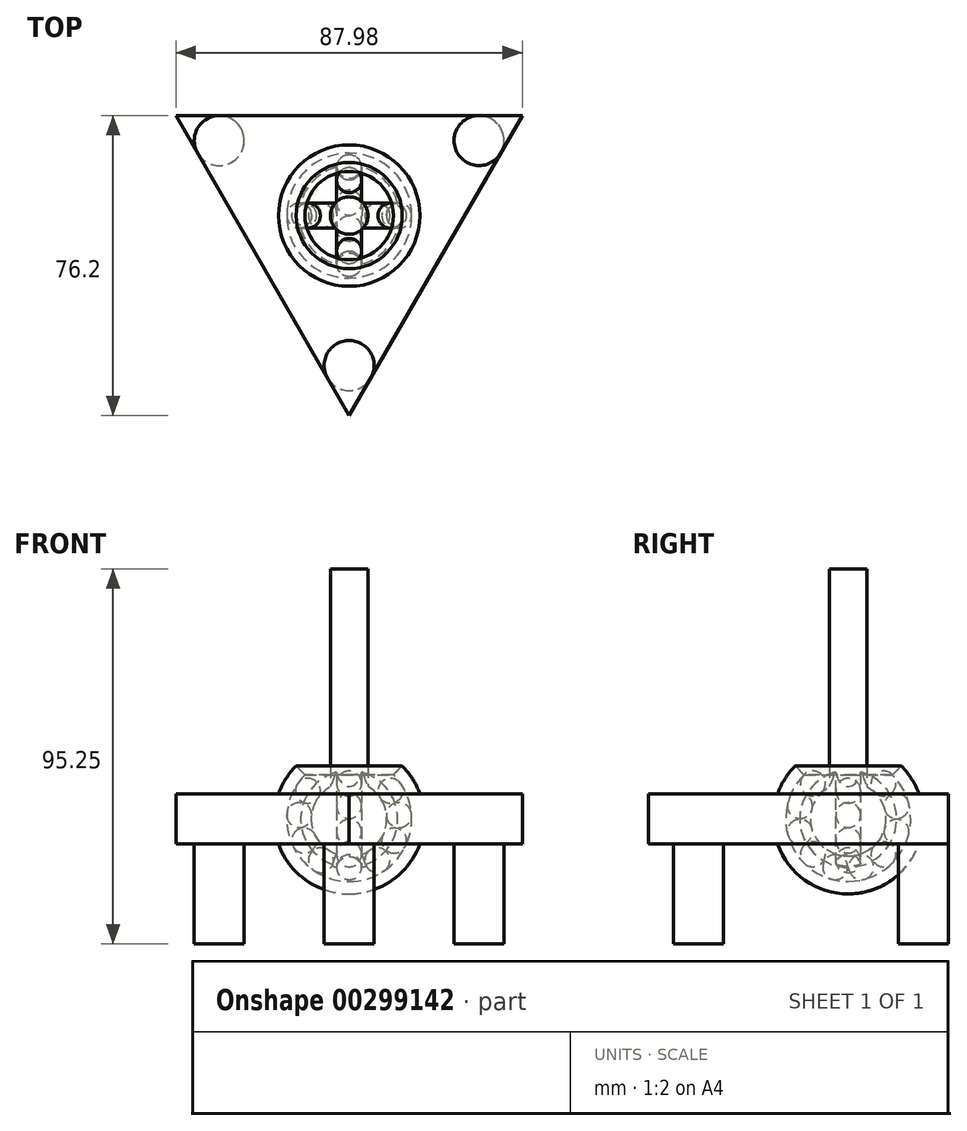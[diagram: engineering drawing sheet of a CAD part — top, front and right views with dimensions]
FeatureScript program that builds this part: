
annotation { "Feature Type Name" : "Feature", "Feature Type Description" : "" }
export const myFeature = defineFeature(function(context is Context, id is Id, definition is map)
    precondition{}
    {
        {
            var Q0;
            Q0=qCreatedBy(makeId("Front.planeOp"),FACE);
            var sketch = newSketch(context, id + "F0", { "sketchPlane" : qUnion([Q0])});
            skArc(sketch, "E0", {"start": v(0, -12.7) * mm, "mid": v(12.7, 0) * mm, "end": v(0, 12.7) * mm});
            skLineSegment(sketch, "E1", {"start": v(0, 12.7) * mm, "end": v(0, -12.7) * mm});
            skSolve(sketch);
        }
        {
            var Q0;
            Q0=makeQuery(id+"F0.imprint","IMPRINT",FACE,{"disambiguationData":[TD([[makeQuery(id+"F0.imprint","IMPRINT",EDGE,{"derivedFrom":sQuery(id+"F0.wireOp",EDGE,"E0")}),1.0]])]});
            var Q1;
            Q1=sQuery(id+"F0.wireOp",EDGE,"E1");
            revolve(context, id + "F1", {"entities" : qUnion([Q0]), "axis" : qUnion([Q1]), "revolveType" : RevolveType.FULL});
        }
        {
            var Q0;
            Q0=qCreatedBy(makeId("Right.planeOp"),FACE);
            var sketch = newSketch(context, id + "F2", { "sketchPlane" : qUnion([Q0])});
            skCircle(sketch, "E2", {"center": v(0, 0) * mm, "radius": 12.7 * mm});
            skSolve(sketch);
        }
        {
            var Q0;
            Q0=qCreatedBy(makeId("Top.planeOp"),FACE);
            var sketch = newSketch(context, id + "F3", { "sketchPlane" : qUnion([Q0])});
            skCircle(sketch, "E3", {"center": v(0, -12.7) * mm, "radius": 3.18 * mm});
            skPoint(sketch, "E4.center", {"position": v(0, 0) * mm});
            skSolve(sketch);
        }
        {
            var Q0;
            Q0=makeQuery(id+"F3.imprint","IMPRINT",FACE,{"disambiguationData":[TD([[makeQuery(id+"F3.imprint","IMPRINT",EDGE,{"derivedFrom":sQuery(id+"F3.wireOp",EDGE,"E3")}),1.0]])]});
            var Q1;
            Q1=sQuery(id+"F2.wireOp",EDGE,"E2");
            revolve(context, id + "F4", {"operationType" : NewBodyOperationType.REMOVE, "entities" : qUnion([Q0]), "axis" : qUnion([Q1]), "revolveType" : RevolveType.FULL, "oppositeDirection" : true});
        }
        {
            var Q0;
            Q0=qCreatedBy(makeId("Right.planeOp"),FACE);
            var sketch = newSketch(context, id + "F5", { "sketchPlane" : qUnion([Q0])});
            skLineSegment(sketch, "E5", {"start": v(0, 0) * mm, "end": v(0, 67.3) * mm, "construction": true});
            skSolve(sketch);
        }
        {
            var Q0;
            Q0=qCreatedBy(makeId("Right.planeOp"),FACE);
            var sketch = newSketch(context, id + "F6", { "sketchPlane" : qUnion([Q0])});
            skArc(sketch, "E6", {"start": v(11.23, 11.23) * mm, "mid": v(6.74, 11.23) * mm, "end": v(6.74, 6.74) * mm});
            skLineSegment(sketch, "E7", {"start": v(8.98, 8.98) * mm, "end": v(0, 0) * mm, "construction": true});
            skLineSegment(sketch, "E8", {"start": v(0, 0) * mm, "end": v(0, 12.71) * mm, "construction": true});
            skLineSegment(sketch, "E9", {"start": v(6.74, 6.74) * mm, "end": v(11.23, 11.23) * mm});
            skSolve(sketch);
        }
        {
            var Q0;
            Q0=makeQuery(id+"F6.imprint","IMPRINT",FACE,{"disambiguationData":[TD([[makeQuery(id+"F6.imprint","IMPRINT",EDGE,{"derivedFrom":sQuery(id+"F6.wireOp",EDGE,"E6")}),1.0]])]});
            var Q1;
            Q1=sQuery(id+"F6.wireOp",EDGE,"E7");
            revolve(context, id + "F7", {"entities" : qUnion([Q0]), "axis" : qUnion([Q1]), "revolveType" : RevolveType.FULL});
        }
        {
            var Q0;
            Q0=makeQuery(id+"F7.opRevolve","SWEPT_BODY",BODY,{"disambiguationData":[OSD([sQuery(id+"F6.wireOp",EDGE,"E6"),sQuery(id+"F6.wireOp",EDGE,"E9")])]});
            var Q1;
            Q1=makeQuery(id+"F4.boolean.opBoolean","COPY",FACE,{"derivedFrom":makeQuery(id+"F4.opRevolve","SWEPT_FACE",FACE,{"disambiguationData":[OSD([sQuery(id+"F3.wireOp",EDGE,"E3")])]})});
            circularPattern(context, id + "F8", {"entities" : qUnion([Q0]), "axis" : qUnion([Q1]), "angle" : 270 * degree, "instanceCount" : 10, "equalSpace" : true});
        }
        {
            var Q0;
            Q0=qCreatedBy(makeId("Top.planeOp"),FACE);
            var sketch = newSketch(context, id + "F9", { "sketchPlane" : qUnion([Q0])});
            skCircle(sketch, "E10", {"center": v(12.7, 0) * mm, "radius": 3.18 * mm});
            skSolve(sketch);
        }
        {
            var Q0;
            Q0=qCreatedBy(makeId("Right.planeOp"),FACE);
            var sketch = newSketch(context, id + "F10", { "sketchPlane" : qUnion([Q0])});
            skLineSegment(sketch, "E11", {"start": v(-25.97, 0) * mm, "end": v(39.67, 0) * mm, "construction": true});
            skSolve(sketch);
        }
        {
            var Q0;
            Q0=makeQuery(id+"F9.imprint","IMPRINT",FACE,{"disambiguationData":[TD([[makeQuery(id+"F9.imprint","IMPRINT",EDGE,{"derivedFrom":sQuery(id+"F9.wireOp",EDGE,"E10")}),1.0]])]});
            var Q1;
            Q1=sQuery(id+"F10.wireOp",EDGE,"E11");
            revolve(context, id + "F11", {"operationType" : NewBodyOperationType.REMOVE, "entities" : qUnion([Q0]), "axis" : qUnion([Q1]), "revolveType" : RevolveType.TWO_DIRECTIONS, "oppositeDirection" : true, "angle" : 250 * degree, "angleBack" : 290 * degree});
        }
        {
            var Q0;
            Q0=qCreatedBy(makeId("Top.planeOp"),FACE);
            var sketch = newSketch(context, id + "F12", { "sketchPlane" : qUnion([Q0])});
            skCircle(sketch, "E12", {"center": v(0, 0) * mm, "radius": 4.76 * mm});
            skSolve(sketch);
        }
        {
            var Q0;
            Q0 = qSketchRegion(id + "F12", true);
            extrude(context, id + "F13", {"entities" : qUnion([Q0]), "operationType" : NewBodyOperationType.ADD, "depth" : 63.5 * mm});
        }
        {
            var Q0;
            Q0=qCreatedBy(makeId("Front.planeOp"),FACE);
            var sketch = newSketch(context, id + "F14", { "sketchPlane" : qUnion([Q0])});
            skArc(sketch, "E13", {"start": v(5.38, -7.86) * mm, "mid": v(4.55, -12.28) * mm, "end": v(8.96, -13.1) * mm});
            skLineSegment(sketch, "E14", {"start": v(7.17, -10.48) * mm, "end": v(0, 0) * mm, "construction": true});
            skLineSegment(sketch, "E15", {"start": v(0, 0) * mm, "end": v(0, -18.63) * mm, "construction": true});
            skLineSegment(sketch, "E16", {"start": v(5.38, -7.86) * mm, "end": v(8.96, -13.1) * mm});
            skSolve(sketch);
        }
        {
            var Q0;
            Q0=qCreatedBy(makeId("Top.planeOp"),FACE);
            var sketch = newSketch(context, id + "F15", { "sketchPlane" : qUnion([Q0])});
            skLineSegment(sketch, "E17", {"start": v(0, 30.24) * mm, "end": v(0, -29.34) * mm, "construction": true});
            skSolve(sketch);
        }
        {
            var Q0;
            Q0 = qSketchRegion(id + "F14", true);
            var Q1;
            Q1=sQuery(id+"F14.wireOp",EDGE,"E14");
            revolve(context, id + "F16", {"entities" : qUnion([Q0]), "axis" : qUnion([Q1]), "revolveType" : RevolveType.FULL});
        }
        {
            var Q0;
            Q0=makeQuery(id+"F16.opRevolve","SWEPT_BODY",BODY,{"disambiguationData":[OSD([sQuery(id+"F14.wireOp",EDGE,"E13"),sQuery(id+"F14.wireOp",EDGE,"E16")])]});
            var Q1;
            Q1=sQuery(id+"F15.wireOp",EDGE,"E17");
            circularPattern(context, id + "F17", {"entities" : qUnion([Q0]), "axis" : qUnion([Q1]), "angle" : 30 * degree, "instanceCount" : 4});
        }
        {
            var Q0;
            Q0=makeQuery(id+"F17.opPattern","COPY",BODY,{"derivedFrom":makeQuery(id+"F16.opRevolve","SWEPT_BODY",BODY,{"disambiguationData":[OSD([sQuery(id+"F14.wireOp",EDGE,"E13"),sQuery(id+"F14.wireOp",EDGE,"E16")])]}),"instanceName":"3"});
            var Q1;
            Q1=makeQuery(id+"F17.opPattern","COPY",BODY,{"derivedFrom":makeQuery(id+"F16.opRevolve","SWEPT_BODY",BODY,{"disambiguationData":[OSD([sQuery(id+"F14.wireOp",EDGE,"E13"),sQuery(id+"F14.wireOp",EDGE,"E16")])]}),"instanceName":"2"});
            var Q2;
            Q2=makeQuery(id+"F16.opRevolve","SWEPT_BODY",BODY,{"disambiguationData":[OSD([sQuery(id+"F14.wireOp",EDGE,"E13"),sQuery(id+"F14.wireOp",EDGE,"E16")])]});
            var Q3;
            Q3=makeQuery(id+"F17.opPattern","COPY",BODY,{"derivedFrom":makeQuery(id+"F16.opRevolve","SWEPT_BODY",BODY,{"disambiguationData":[OSD([sQuery(id+"F14.wireOp",EDGE,"E13"),sQuery(id+"F14.wireOp",EDGE,"E16")])]}),"instanceName":"1"});
            var Q4;
            Q4=qCreatedBy(makeId("Right.planeOp"),FACE);
            mirror(context, id + "F18", {"entities" : qUnion([Q0, Q1, Q2, Q3]), "mirrorPlane" : qUnion([Q4])});
        }
        {
            var Q0;
            Q0=qCreatedBy(makeId("Right.planeOp"),FACE);
            var sketch = newSketch(context, id + "F19", { "sketchPlane" : qUnion([Q0])});
            skLineSegment(sketch, "E18", {"start": v(0, -15.87) * mm, "end": v(0, -19.05) * mm});
            skArc(sketch, "E19", {"start": v(0, -15.87) * mm, "mid": v(14.67, -6.08) * mm, "end": v(11.23, 11.23) * mm});
            skArc(sketch, "E20", {"start": v(0, -19.05) * mm, "mid": v(17.6, -7.3) * mm, "end": v(13.47, 13.47) * mm});
            skLineSegment(sketch, "E21", {"start": v(11.23, 11.23) * mm, "end": v(13.47, 13.47) * mm});
            skLineSegment(sketch, "E22", {"start": v(13.47, 13.47) * mm, "end": v(0, 0) * mm, "construction": true});
            skSolve(sketch);
        }
        {
            var Q0;
            Q0 = qSketchRegion(id + "F19", true);
            var Q1;
            Q1=sQuery(id+"F19.wireOp",EDGE,"E18");
            revolve(context, id + "F20", {"entities" : qUnion([Q0]), "axis" : qUnion([Q1]), "revolveType" : RevolveType.FULL});
        }
        {
            var Q0;
            Q0=qCreatedBy(makeId("Top.planeOp"),FACE);
            var sketch = newSketch(context, id + "F21", { "sketchPlane" : qUnion([Q0])});
            skLineSegment(sketch, "E23", {"start": v(0, -50.8) * mm, "end": v(44, 25.4) * mm});
            skLineSegment(sketch, "E24", {"start": v(44, 25.4) * mm, "end": v(-44, 25.4) * mm});
            skLineSegment(sketch, "E25", {"start": v(-44, 25.4) * mm, "end": v(0, -50.8) * mm});
            skCircle(sketch, "E26", {"center": v(0, 0) * mm, "radius": 17.46 * mm});
            skSolve(sketch);
        }
        {
            var Q0;
            Q0=makeQuery(id+"F21.imprint","IMPRINT",FACE,{"disambiguationData":[TD([[makeQuery(id+"F21.imprint","IMPRINT",EDGE,{"derivedFrom":sQuery(id+"F21.wireOp",EDGE,"E23")}),1.0]])]});
            extrude(context, id + "F22", {"entities" : qUnion([Q0]), "operationType" : NewBodyOperationType.ADD, "depth" : 12.7 * mm, "symmetric" : true});
        }
        {
            var Q0;
            Q0=makeQuery(id+"F22.opExtrude","CAP_FACE",FACE,{"disambiguationData":[OSD([sQuery(id+"F21.wireOp",EDGE,"E23"),sQuery(id+"F21.wireOp",EDGE,"E24"),sQuery(id+"F21.wireOp",EDGE,"E25"),sQuery(id+"F21.wireOp",EDGE,"E26")])],"isStart":true});
            var sketch = newSketch(context, id + "F23", { "sketchPlane" : qUnion([Q0])});
            skCircle(sketch, "E27", {"center": v(0, 38.1) * mm, "radius": 6.35 * mm});
            skCircle(sketch, "E28", {"center": v(0, 0) * mm, "radius": 31.75 * mm, "construction": true});
            skCircle(sketch, "E29.1.0", {"center": v(-33, -19.05) * mm, "radius": 6.35 * mm});
            skCircle(sketch, "E29.2.0", {"center": v(33, -19.05) * mm, "radius": 6.35 * mm});
            skSolve(sketch);
        }
        {
            var Q0;
            Q0 = qSketchRegion(id + "F23", true);
            extrude(context, id + "F24", {"entities" : qUnion([Q0]), "depth" : 25.4 * mm});
        }
    });
